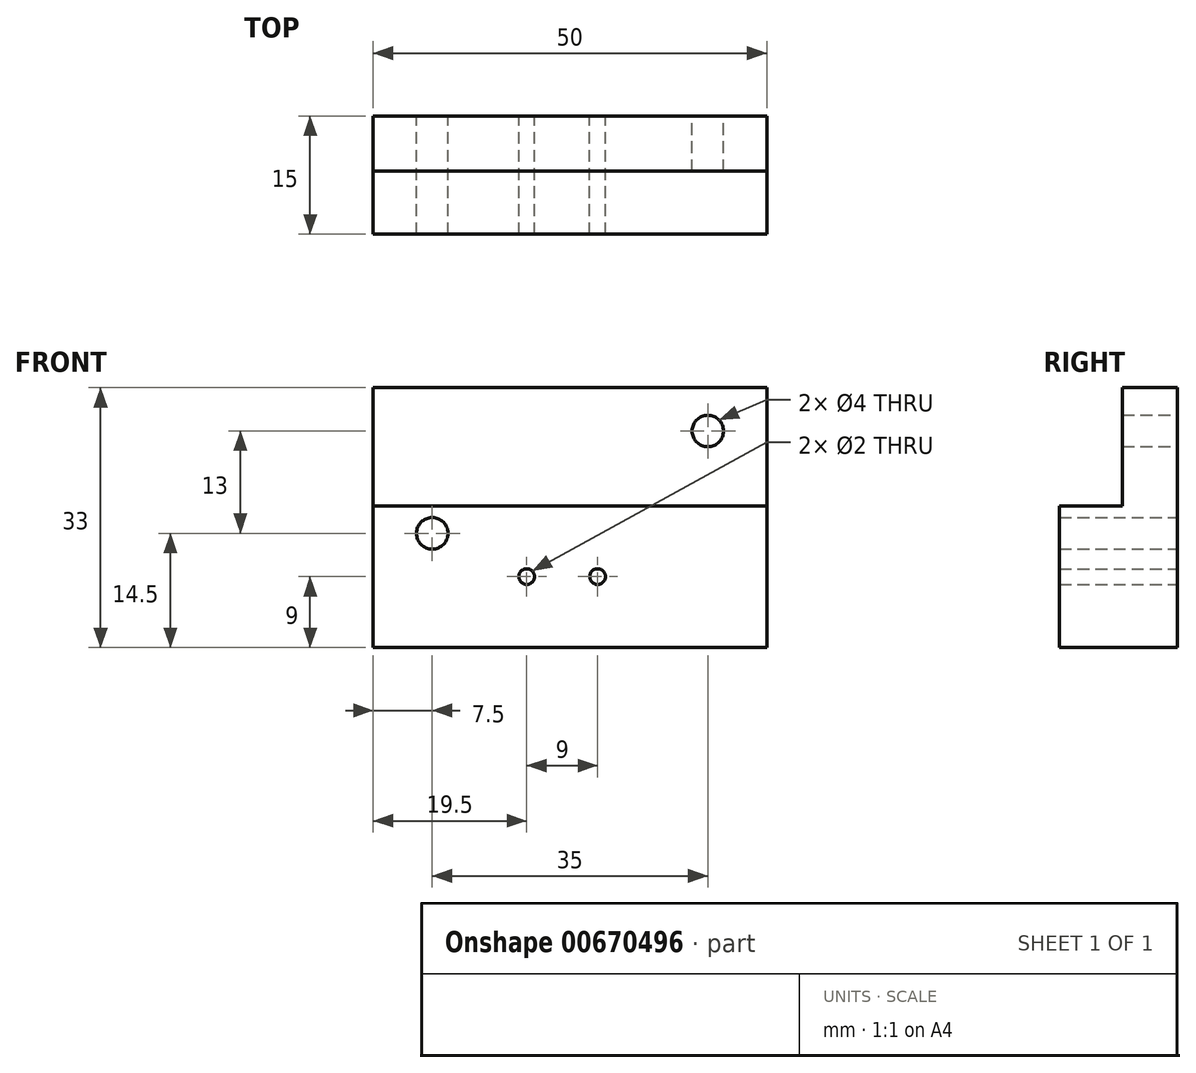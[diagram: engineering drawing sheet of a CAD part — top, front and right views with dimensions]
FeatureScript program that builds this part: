
annotation { "Feature Type Name" : "Feature", "Feature Type Description" : "" }
export const myFeature = defineFeature(function(context is Context, id is Id, definition is map)
    precondition{}
    {
        {
            var Q0;
            Q0=qCreatedBy(makeId("Front.planeOp"),FACE);
            var sketch = newSketch(context, id + "F0", { "sketchPlane" : qUnion([Q0])});
            skLineSegment(sketch, "E0.bottom", {"start": v(0, 0) * mm, "end": v(50, 0) * mm});
            skLineSegment(sketch, "E0.top", {"start": v(0, -33) * mm, "end": v(50, -33) * mm});
            skLineSegment(sketch, "E0.left", {"start": v(0, 0) * mm, "end": v(0, -33) * mm});
            skLineSegment(sketch, "E0.right", {"start": v(50, 0) * mm, "end": v(50, -33) * mm});
            skPoint(sketch, "E1", {"position": v(7.5, 0) * mm});
            skPoint(sketch, "E2", {"position": v(0.1, -18.5) * mm});
            skCircle(sketch, "E3", {"center": v(7.5, -18.5) * mm, "radius": 2 * mm});
            skPoint(sketch, "E4", {"position": v(42.5, 0) * mm});
            skPoint(sketch, "E5", {"position": v(50, -5.5) * mm});
            skCircle(sketch, "E6", {"center": v(42.5, -5.5) * mm, "radius": 2 * mm});
            skPoint(sketch, "E7", {"position": v(19.5, 0) * mm});
            skPoint(sketch, "E8", {"position": v(0, -24) * mm});
            skCircle(sketch, "E9", {"center": v(19.5, -24) * mm, "radius": 1 * mm});
            skCircle(sketch, "E10", {"center": v(28.5, -24) * mm, "radius": 1 * mm});
            skSolve(sketch);
        }
        {
            var Q0;
            Q0=makeQuery(id+"F0.imprint","IMPRINT",FACE,{"disambiguationData":[TD([[makeQuery(id+"F0.imprint","IMPRINT",EDGE,{"derivedFrom":sQuery(id+"F0.wireOp",EDGE,"E0.bottom")}),-1.0]])]});
            extrude(context, id + "F1", {"entities" : qUnion([Q0]), "depth" : 7 * mm, "offsetDistance" : 25 * mm});
        }
        {
            var Q0;
            Q0=qCreatedBy(makeId("Front.planeOp"),FACE);
            var sketch = newSketch(context, id + "F2", { "sketchPlane" : qUnion([Q0])});
            skLineSegment(sketch, "E11.bottom", {"start": v(0, -15) * mm, "end": v(50, -15) * mm});
            skLineSegment(sketch, "E11.top", {"start": v(0, -33) * mm, "end": v(50, -33) * mm});
            skLineSegment(sketch, "E11.left", {"start": v(0, -15) * mm, "end": v(0, -33) * mm});
            skLineSegment(sketch, "E11.right", {"start": v(50, -15) * mm, "end": v(50, -33) * mm});
            skPoint(sketch, "E12", {"position": v(7.5, -15) * mm});
            skPoint(sketch, "E13", {"position": v(0, -18.5) * mm});
            skCircle(sketch, "E14", {"center": v(7.5, -18.5) * mm, "radius": 2 * mm});
            skPoint(sketch, "E15", {"position": v(19.5, -15) * mm});
            skPoint(sketch, "E16", {"position": v(0, -24) * mm});
            skCircle(sketch, "E17", {"center": v(19.5, -24) * mm, "radius": 1 * mm});
            skCircle(sketch, "E18", {"center": v(28.5, -24) * mm, "radius": 1 * mm});
            skSolve(sketch);
        }
        {
            var Q0;
            Q0 = qSketchRegion(id + "F2", true);
            extrude(context, id + "F3", {"entities" : qUnion([Q0]), "operationType" : NewBodyOperationType.ADD, "depth" : 15 * mm, "offsetDistance" : 25 * mm});
        }
    });
